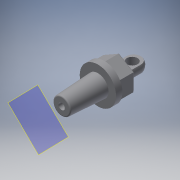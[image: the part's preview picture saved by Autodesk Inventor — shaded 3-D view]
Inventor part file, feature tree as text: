
AUTODESK INVENTOR PART (.ipt)
format: ipt  version: 2016 (Build 200138000, 138)  size: 188,928 bytes
history: native  units: mm
features: extrude x7, sketch x7, fillet x4, draft x1, plane x1
ambient origin geometry x8: Origin, YZ Plane, XZ Plane, XY Plane, X Axis, Y Axis, Z Axis, Center Point
bodies: Solid1 (feature_tree)
feature tree (20):
  extrude  "Extrusion1"  Depth=17.0mm TaperAngle=0.0deg
  extrude  "Extrusion2"  Depth=7.0mm TaperAngle=0.0deg
  fillet  "Fillet1"  Radius=0.5mm
  extrude  "Extrusion3"  Depth=0.8mm TaperAngle=0.0deg
  extrude  "Extrusion4"  Depth=9.8mm TaperAngle=0.0deg
  extrude  "Extrusion5"  Depth=5.0mm
  fillet  "Fillet3"  Radius=3.406614mm
  extrude  "Extrusion6"  Depth=9.8mm TaperAngle=0.0deg
  draft  "FaceDraft1"
  extrude  "Extrusion7"  Depth=10.0mm
  fillet  "Fillet4"  Radius=17.0mm
  plane  "Work Plane1"
  fillet  "Fillet5"  Radius=0.523599mm
  sketch  "Sketch1"  dims[d0=17.0mm d1=3.0mm d2=0.0mm]
  sketch  "Sketch2"  dims[d3=14.0mm d4=7.0mm d5=0.0mm d6=0.5mm]
  sketch  "Sketch3"  dims[d7=7.7mm d8=0.8mm d9=0.0mm]
  sketch  "Sketch4"  dims[d11=3.6mm d12=9.8mm d13=0.0mm]
  sketch  "Sketch5"  dims[d15=5.0mm d16=3.4mm d17=3.406614mm]
  sketch  "Sketch6"  dims[d18=4.5mm d19=9.8mm d20=0.0mm]
  sketch  "Sketch8"  dims[d21=3.85mm d22=10.0mm d23=17.0mm d24=0.0mm d25=0.523599mm d26=3.0mm d27=15.0mm d28=0.0mm d29=0.3mm d30=0.6mm]
